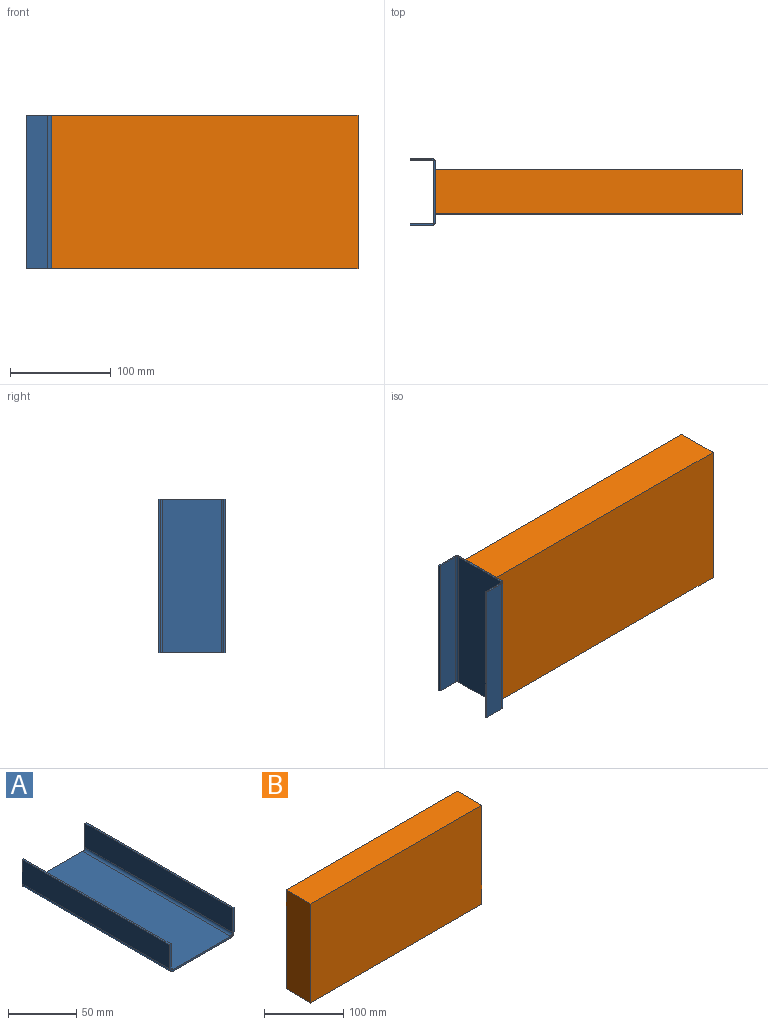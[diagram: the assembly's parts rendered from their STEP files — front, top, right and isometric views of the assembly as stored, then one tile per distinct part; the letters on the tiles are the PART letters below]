
ASSEMBLY  parts=2 mates=2
PART A: 22 faces, bbox 66.7x152.4x25.4 mm
  f0: plane 58.93x1.59mm, normal (0,1,0), area 93.5mm2, adj f2,f3,f9,f18
  f1: plane 58.93x1.59mm, normal (0,-1,0), area 93.5mm2, adj f2,f3,f10,f19
  f2: plane 152.4x58.93mm, normal (0,0,-1), area 8980.6mm2, adj f0,f1,f11,f20
  f3: plane 152.4x58.93mm, normal (0,0,1), area 8980.6mm2, adj f0,f1,f12,f21
  f4: plane 152.4x1.59mm, normal (0,0,1), area 241.9mm2, adj f5,f6,f7,f8
  f5: plane 21.53x1.59mm, normal (0,-1,0), area 34.2mm2, adj f4,f7,f8,f10
  f6: plane 21.53x1.59mm, normal (0,1,0), area 34.2mm2, adj f4,f7,f8,f9
  f7: plane 152.4x21.53mm, normal (1,0,0), area 3280.6mm2, adj f4,f5,f6,f11
  f8: plane 152.4x21.53mm, normal (-1,0,0), area 3280.6mm2, adj f4,f5,f6,f12
  f9: plane 3.87x3.87mm, normal (0,1,0), area 7.7mm2, adj f0,f6,f11,f12
  f10: plane 3.87x3.87mm, normal (0,-1,0), area 7.7mm2, adj f1,f5,f11,f12
  f11: cylinder r=3.87mm len=152.4mm, axis (0,1,0), area 927.3mm2, adj f2,f7,f9,f10
  f12: cylinder r=2.29mm len=152.4mm, axis (0,1,0), area 547.2mm2, adj f3,f8,f9,f10
  f13: plane 152.4x1.59mm, normal (0,0,1), area 241.9mm2, adj f14,f15,f16,f17
  f14: plane 21.53x1.59mm, normal (0,1,0), area 34.2mm2, adj f13,f16,f17,f18
  f15: plane 21.53x1.59mm, normal (0,-1,0), area 34.2mm2, adj f13,f16,f17,f19
  f16: plane 152.4x21.53mm, normal (-1,0,0), area 3280.6mm2, adj f13,f14,f15,f20
  f17: plane 152.4x21.53mm, normal (1,0,0), area 3280.6mm2, adj f13,f14,f15,f21
  f18: plane 3.87x3.87mm, normal (0,1,0), area 7.7mm2, adj f0,f14,f20,f21
  f19: plane 3.87x3.87mm, normal (0,-1,0), area 7.7mm2, adj f1,f15,f20,f21
  f20: cylinder r=3.87mm len=152.4mm, axis (0,1,0), area 927.3mm2, adj f2,f16,f18,f19
  f21: cylinder r=2.29mm len=152.4mm, axis (0,1,0), area 547.2mm2, adj f3,f17,f18,f19
PART B: 6 faces, bbox 304.8x44x152.4 mm
  f0: plane 304.8x152.4mm, normal (0,1,0), area 46451.5mm2, adj f1,f3,f4,f5
  f1: plane 304.8x43.99mm, normal (0,0,1), area 13409mm2, adj f0,f2,f4,f5
  f2: plane 304.8x152.4mm, normal (0,-1,0), area 46451.5mm2, adj f1,f3,f4,f5
  f3: plane 304.8x43.99mm, normal (0,0,-1), area 13409mm2, adj f0,f2,f4,f5
  f4: plane 152.4x43.99mm, normal (1,0,0), area 6704.5mm2, adj f0,f1,f2,f3
  f5: plane 152.4x43.99mm, normal (-1,0,0), area 6704.5mm2, adj f0,f1,f2,f3
PLACE A rot(axis=(-0.58,-0.58,0.58),120deg) t=(-152.58,-0.1,0)mm
PLACE B t=(-0.18,-0.1,0)mm
MATE planar A.f2 <-> B.f5  axis (1,0,0) through (-152.58,29.36,0)mm
MATE planar A.f1 <-> B.f1  axis (0,0,1) through (-153.37,-0.1,76.2)mm
